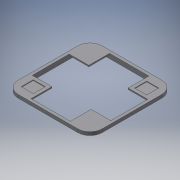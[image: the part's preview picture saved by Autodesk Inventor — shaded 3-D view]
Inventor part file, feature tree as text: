
AUTODESK INVENTOR PART (.ipt)
format: ipt  version: 2016 SP2 (Build 200236200, 236)  size: 182,784 bytes
history: native  units: mm
features: reference x7, extrude x3, sketch x3, chamfer x1
ambient origin geometry x8: Origin, YZ Plane, XZ Plane, XY Plane, X Axis, Y Axis, Z Axis, Center Point
bodies: Volumenkörper1 (feature_tree)
feature tree (14):
  extrude  "Extrusion1"  Depth=3.0mm
  chamfer  "Fase1"  Distance=12.0mm
  extrude  "Extrusion2"  Depth=0.8mm
  extrude  "Extrusion3"  Depth=5.0mm TaperAngle=0.0deg
  sketch  "Skizze1"  dims[d0=0.18mm d1=3.0mm]
  reference  "Referenz1"
  reference  "Referenz2"
  reference  "Referenz3"
  sketch  "Skizze2"  dims[d2=12.0mm]
  reference  "Referenz4"
  reference  "Referenz5"
  sketch  "Skizze3"  dims[d3=12.0mm d4=12.0mm d5=12.0mm d6=5.0mm d7=0.0mm d8=2.0mm d9=2.0mm d10=6.108652mm d11=10.0mm d12=10.0mm d13=10.0mm d14=10.0mm d15=1.4mm d16=0.0mm d17=13.0mm d18=13.0mm d19=13.0mm d20=13.0mm d21=0.8mm d22=0.0mm]
  reference  "Referenz6"
  reference  "Referenz7"
